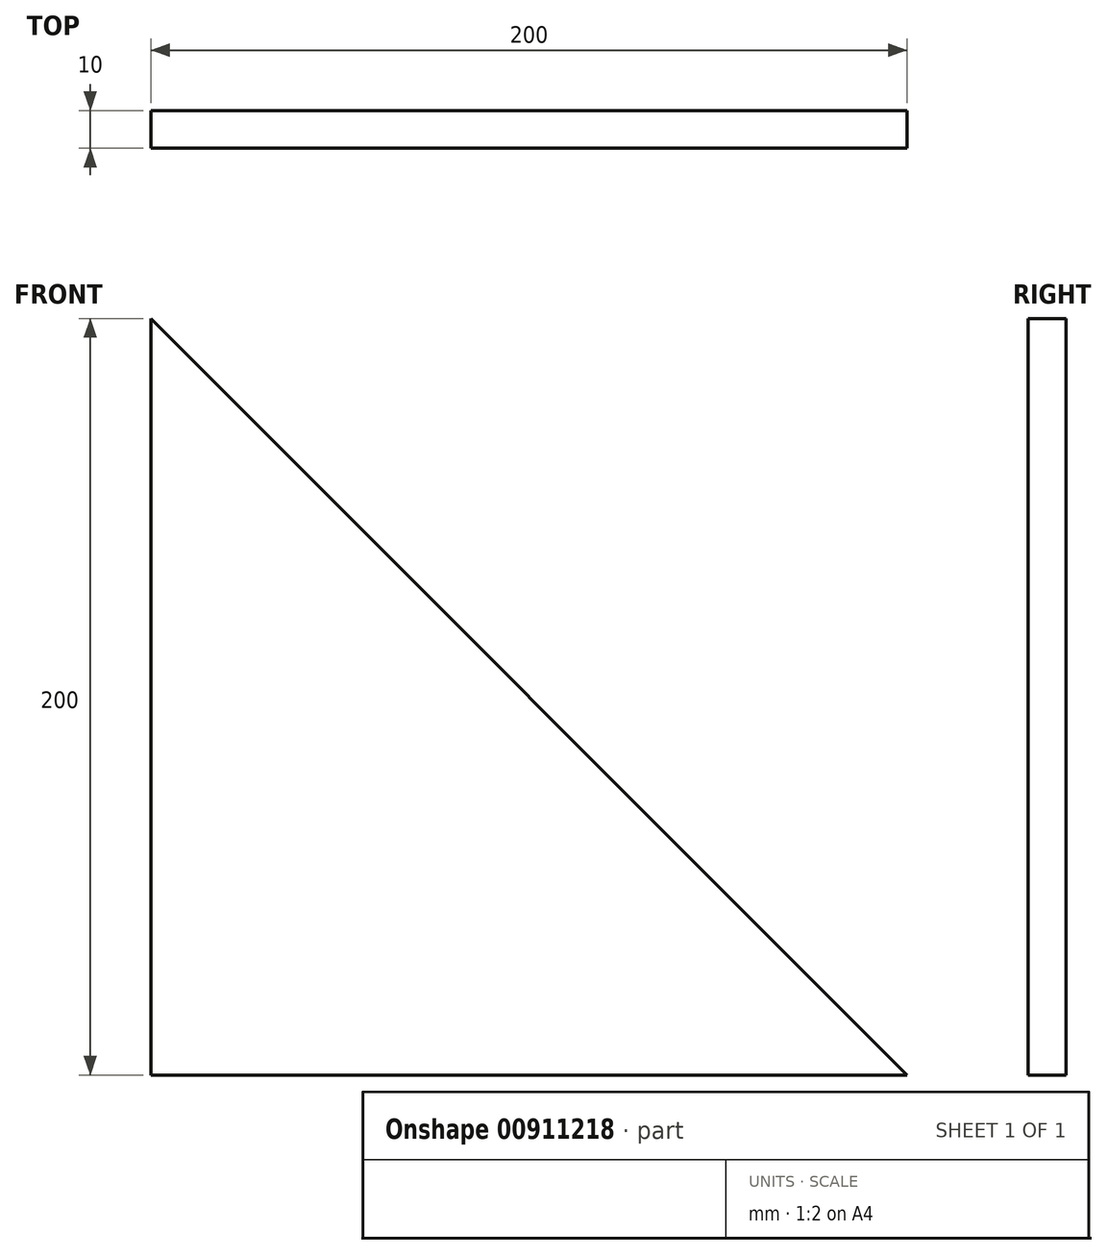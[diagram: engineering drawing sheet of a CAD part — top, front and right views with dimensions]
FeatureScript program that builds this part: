
annotation { "Feature Type Name" : "Feature", "Feature Type Description" : "" }
export const myFeature = defineFeature(function(context is Context, id is Id, definition is map)
    precondition{}
    {
        {
            var Q0;
            Q0=qCreatedBy(makeId("Front.planeOp"),FACE);
            var sketch = newSketch(context, id + "F0", { "sketchPlane" : qUnion([Q0])});
            skLineSegment(sketch, "E0", {"start": v(0, 0) * mm, "end": v(200, 0) * mm});
            skLineSegment(sketch, "E1", {"start": v(0, 0) * mm, "end": v(0, 200) * mm});
            skLineSegment(sketch, "E2", {"start": v(0, 200) * mm, "end": v(200, 0) * mm});
            skSolve(sketch);
        }
        {
            var Q0;
            Q0=makeQuery(id+"F0.imprint","IMPRINT",FACE,{"disambiguationData":[TD([[makeQuery(id+"F0.imprint","IMPRINT",EDGE,{"derivedFrom":sQuery(id+"F0.wireOp",EDGE,"E0")}),1.0]])]});
            extrude(context, id + "F1", {"entities" : qUnion([Q0]), "depth" : 10 * mm, "offsetDistance" : 25 * mm});
        }
    });
